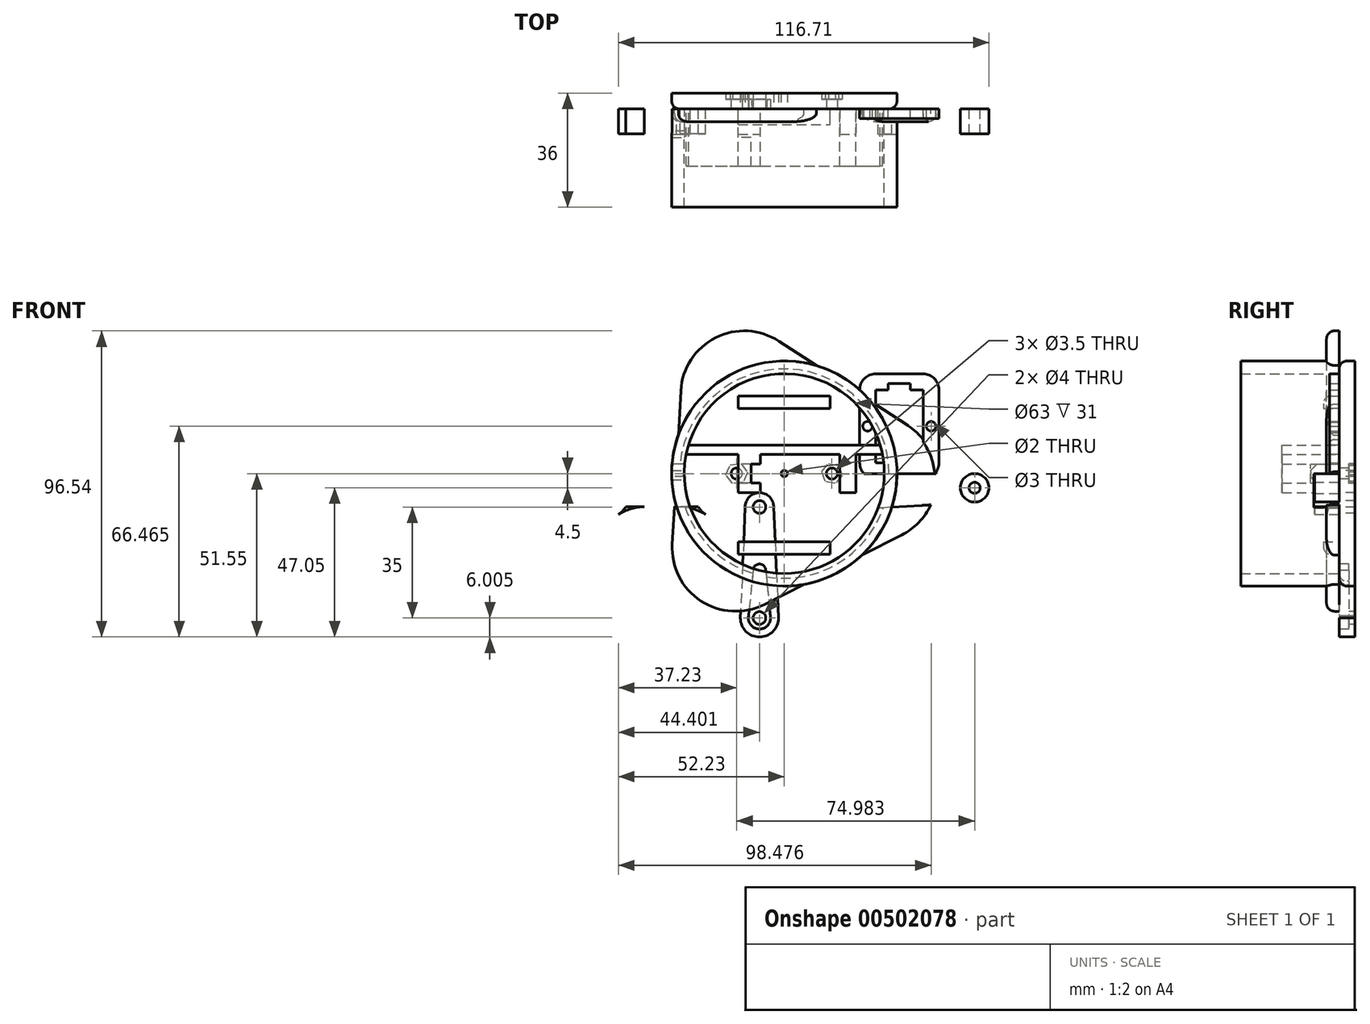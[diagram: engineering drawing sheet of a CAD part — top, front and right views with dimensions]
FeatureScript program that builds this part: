
annotation { "Feature Type Name" : "Feature", "Feature Type Description" : "" }
export const myFeature = defineFeature(function(context is Context, id is Id, definition is map)
    precondition{}
    {
        {
            var Q0;
            Q0=qCreatedBy(makeId("Front.planeOp"),FACE);
            var sketch = newSketch(context, id + "F0", { "sketchPlane" : qUnion([Q0])});
            skCircle(sketch, "E0", {"center": v(0, 0) * mm, "radius": 35.5 * mm});
            skLineSegment(sketch, "E1.bottom", {"start": v(-14.5, 24.48) * mm, "end": v(14.5, 24.48) * mm});
            skLineSegment(sketch, "E1.top", {"start": v(-14.5, 20.48) * mm, "end": v(14.5, 20.48) * mm});
            skLineSegment(sketch, "E1.left", {"start": v(-14.5, 24.48) * mm, "end": v(-14.5, 20.48) * mm});
            skLineSegment(sketch, "E1.right", {"start": v(14.5, 24.48) * mm, "end": v(14.5, 20.48) * mm});
            skLineSegment(sketch, "E2.bottom", {"start": v(-14.5, -21.52) * mm, "end": v(14.5, -21.52) * mm});
            skLineSegment(sketch, "E2.top", {"start": v(-14.5, -25.52) * mm, "end": v(14.5, -25.52) * mm});
            skLineSegment(sketch, "E2.left", {"start": v(-14.5, -21.52) * mm, "end": v(-14.5, -25.52) * mm});
            skLineSegment(sketch, "E2.right", {"start": v(14.5, -21.52) * mm, "end": v(14.5, -25.52) * mm});
            skCircle(sketch, "E3", {"center": v(0, 0) * mm, "radius": 1 * mm});
            skCircle(sketch, "E4", {"center": v(15, 0) * mm, "radius": 1.75 * mm});
            skCircle(sketch, "E5", {"center": v(-15, 0) * mm, "radius": 1.75 * mm});
            skLineSegment(sketch, "E6.0", {"start": v(17.15, 2.5) * mm, "end": v(18.24, -0.61) * mm});
            skLineSegment(sketch, "E6.1", {"start": v(18.24, -0.61) * mm, "end": v(16.09, -3.1) * mm});
            skLineSegment(sketch, "E6.2", {"start": v(16.09, -3.1) * mm, "end": v(12.85, -2.5) * mm});
            skLineSegment(sketch, "E6.3", {"start": v(12.85, -2.5) * mm, "end": v(11.76, 0.61) * mm});
            skLineSegment(sketch, "E6.4", {"start": v(11.76, 0.61) * mm, "end": v(13.91, 3.1) * mm});
            skLineSegment(sketch, "E6.5", {"start": v(13.91, 3.1) * mm, "end": v(17.15, 2.5) * mm});
            skPoint(sketch, "E6.0.midPoint", {"position": v(17.7, 0.94) * mm});
            skLineSegment(sketch, "E7.0", {"start": v(-13.66, 3.16) * mm, "end": v(-11.6, 0.41) * mm});
            skLineSegment(sketch, "E7.1", {"start": v(-11.6, 0.41) * mm, "end": v(-12.94, -2.74) * mm});
            skLineSegment(sketch, "E7.2", {"start": v(-12.94, -2.74) * mm, "end": v(-16.34, -3.16) * mm});
            skLineSegment(sketch, "E7.3", {"start": v(-16.34, -3.16) * mm, "end": v(-18.4, -0.41) * mm});
            skLineSegment(sketch, "E7.4", {"start": v(-18.4, -0.41) * mm, "end": v(-17.06, 2.74) * mm});
            skLineSegment(sketch, "E7.5", {"start": v(-17.06, 2.74) * mm, "end": v(-13.66, 3.16) * mm});
            skPoint(sketch, "E7.0.midPoint", {"position": v(-12.63, 1.78) * mm});
            skSolve(sketch);
        }
        {
            var Q0;
            Q0=makeQuery(id+"F0.imprint","IMPRINT",FACE,{"disambiguationData":[TD([[makeQuery(id+"F0.imprint","IMPRINT",EDGE,{"derivedFrom":sQuery(id+"F0.wireOp",EDGE,"E0")}),1.0]])]});
            var Q1;
            Q1=makeQuery(id+"F0.imprint","IMPRINT",FACE,{"disambiguationData":[TD([[makeQuery(id+"F0.imprint","IMPRINT",EDGE,{"derivedFrom":sQuery(id+"F0.wireOp",EDGE,"E1.bottom")}),-1.0]])]});
            var Q2;
            Q2=makeQuery(id+"F0.imprint","IMPRINT",FACE,{"disambiguationData":[TD([[makeQuery(id+"F0.imprint","IMPRINT",EDGE,{"derivedFrom":sQuery(id+"F0.wireOp",EDGE,"E2.bottom")}),-1.0]])]});
            extrude(context, id + "F1", {"entities" : qUnion([Q0, Q1, Q2]), "depth" : -5 * mm});
        }
        {
            var Q0;
            Q0=makeQuery(id+"F0.imprint","IMPRINT",FACE,{"disambiguationData":[TD([[makeQuery(id+"F0.imprint","IMPRINT",EDGE,{"derivedFrom":sQuery(id+"F0.wireOp",EDGE,"E1.bottom")}),-1.0]])]});
            var Q1;
            Q1=makeQuery(id+"F0.imprint","IMPRINT",FACE,{"disambiguationData":[TD([[makeQuery(id+"F0.imprint","IMPRINT",EDGE,{"derivedFrom":sQuery(id+"F0.wireOp",EDGE,"E2.bottom")}),-1.0]])]});
            extrude(context, id + "F2", {"entities" : qUnion([Q0, Q1]), "operationType" : NewBodyOperationType.ADD, "depth" : 5 * mm});
        }
        {
            var Q0;
            Q0=makeQuery(id+"F0.imprint","IMPRINT",FACE,{"disambiguationData":[TD([[makeQuery(id+"F0.imprint","IMPRINT",EDGE,{"derivedFrom":sQuery(id+"F0.wireOp",EDGE,"E4")}),-1.0]])]});
            var Q1;
            Q1=makeQuery(id+"F0.imprint","IMPRINT",FACE,{"disambiguationData":[TD([[makeQuery(id+"F0.imprint","IMPRINT",EDGE,{"derivedFrom":sQuery(id+"F0.wireOp",EDGE,"E5")}),-1.0]])]});
            extrude(context, id + "F3", {"entities" : qUnion([Q0, Q1]), "operationType" : NewBodyOperationType.ADD, "depth" : -3 * mm});
        }
        {
            var Q0;
            Q0=qCreatedBy(makeId("Front.planeOp"),FACE);
            var sketch = newSketch(context, id + "F4", { "sketchPlane" : qUnion([Q0])});
            skLineSegment(sketch, "E8.bottom", {"start": v(28.75, 31.42) * mm, "end": v(43.75, 31.42) * mm});
            skLineSegment(sketch, "E8.top", {"start": v(28.75, -1.58) * mm, "end": v(43.75, -1.58) * mm});
            skLineSegment(sketch, "E8.left", {"start": v(23.75, 26.42) * mm, "end": v(23.75, 3.42) * mm});
            skLineSegment(sketch, "E8.right", {"start": v(48.75, 26.42) * mm, "end": v(48.75, 3.42) * mm});
            skPoint(sketch, "E9.visualSharp", {"position": v(48.75, 31.42) * mm});
            skArc(sketch, "E9.filletArc", {"start": v(48.75, 26.42) * mm, "mid": v(47.28, 29.95) * mm, "end": v(43.75, 31.42) * mm});
            skPoint(sketch, "E10.visualSharp", {"position": v(23.75, 31.42) * mm});
            skArc(sketch, "E10.filletArc", {"start": v(28.75, 31.42) * mm, "mid": v(25.21, 29.95) * mm, "end": v(23.75, 26.42) * mm});
            skPoint(sketch, "E11.visualSharp", {"position": v(48.75, -1.58) * mm});
            skArc(sketch, "E11.filletArc", {"start": v(43.75, -1.58) * mm, "mid": v(47.28, -0.12) * mm, "end": v(48.75, 3.42) * mm});
            skPoint(sketch, "E12.visualSharp", {"position": v(23.75, -1.58) * mm});
            skArc(sketch, "E12.filletArc", {"start": v(23.75, 3.42) * mm, "mid": v(25.21, -0.12) * mm, "end": v(28.75, -1.58) * mm});
            skLineSegment(sketch, "E13", {"start": v(28.75, 26.42) * mm, "end": v(28.75, 3.42) * mm});
            skLineSegment(sketch, "E14", {"start": v(43.75, 3.42) * mm, "end": v(43.75, 26.42) * mm});
            skLineSegment(sketch, "E15", {"start": v(39.75, 26.42) * mm, "end": v(43.75, 26.42) * mm});
            skLineSegment(sketch, "E16", {"start": v(28.75, 26.42) * mm, "end": v(32.75, 26.42) * mm});
            skLineSegment(sketch, "E17", {"start": v(32.75, 26.42) * mm, "end": v(32.75, 28.42) * mm});
            skLineSegment(sketch, "E18", {"start": v(32.75, 28.42) * mm, "end": v(39.75, 28.42) * mm});
            skLineSegment(sketch, "E19", {"start": v(39.75, 28.42) * mm, "end": v(39.75, 26.42) * mm});
            skCircle(sketch, "E20", {"center": v(26.25, 14.92) * mm, "radius": 1.5 * mm});
            skPoint(sketch, "E20.centerSnap0", {"position": v(23.75, 14.92) * mm});
            skPoint(sketch, "E21.centerSnap0", {"position": v(48.75, 14.92) * mm});
            skLineSegment(sketch, "E22", {"start": v(28.75, 3.42) * mm, "end": v(43.75, 3.42) * mm});
            skCircle(sketch, "E23", {"center": v(46.25, 14.92) * mm, "radius": 1.5 * mm});
            skSolve(sketch);
        }
        {
            var Q0;
            Q0=makeQuery(id+"F4.imprint","IMPRINT",FACE,{"disambiguationData":[TD([[makeQuery(id+"F4.imprint","IMPRINT",EDGE,{"derivedFrom":sQuery(id+"F4.wireOp",EDGE,"E8.bottom")}),-1.0]])]});
            extrude(context, id + "F5", {"entities" : qUnion([Q0]), "depth" : 3 * mm});
        }
        {
            var Q0;
            Q0=qCreatedBy(makeId("Front.planeOp"),FACE);
            var sketch = newSketch(context, id + "F6", { "sketchPlane" : qUnion([Q0])});
            skCircle(sketch, "E24", {"center": v(-7.83, -45.55) * mm, "radius": 6 * mm});
            skCircle(sketch, "E25", {"center": v(-7.83, -10.55) * mm, "radius": 4.5 * mm});
            skLineSegment(sketch, "E26", {"start": v(-3.33, -10.55) * mm, "end": v(-1.83, -45.55) * mm});
            skLineSegment(sketch, "E27", {"start": v(-12.33, -10.55) * mm, "end": v(-13.83, -45.55) * mm});
            skCircle(sketch, "E28", {"center": v(-7.83, -10.55) * mm, "radius": 2 * mm});
            skCircle(sketch, "E29", {"center": v(-7.83, -45.55) * mm, "radius": 2 * mm});
            skCircle(sketch, "E30", {"center": v(-7.83, -45.55) * mm, "radius": 3.5 * mm});
            skCircle(sketch, "E31", {"center": v(-7.83, -30.55) * mm, "radius": 2 * mm});
            skLineSegment(sketch, "E32", {"start": v(-5.83, -30.55) * mm, "end": v(-4.31, -45.55) * mm});
            skLineSegment(sketch, "E33", {"start": v(-9.83, -30.55) * mm, "end": v(-11.33, -45.55) * mm});
            skCircle(sketch, "E34", {"center": v(-7.83, -30.55) * mm, "radius": 3.5 * mm});
            skLineSegment(sketch, "E35", {"start": v(-5.27, -14.25) * mm, "end": v(-4.63, -29.25) * mm});
            skLineSegment(sketch, "E36", {"start": v(-10.39, -14.25) * mm, "end": v(-11.03, -29.25) * mm});
            skSolve(sketch);
        }
        {
            var Q0;
            Q0=makeQuery(id+"F2.opExtrude","CAP_EDGE",EDGE,{"disambiguationData":[OSD([sQuery(id+"F0.wireOp",EDGE,"E2.top")])],"isStart":false});
            var Q1;
            Q1=makeQuery(id+"F2.opExtrude","CAP_EDGE",EDGE,{"disambiguationData":[OSD([sQuery(id+"F0.wireOp",EDGE,"E2.top")])],"isStart":true});
            fillet(context, id + "F7", {"entities" : qUnion([Q0, Q1]), "radius" : 2.5 * mm, "tangentPropagation" : true, "allowEdgeOverflow" : false});
        }
        {
            var Q0;
            Q0=makeQuery(id+"F2.opExtrude","CAP_EDGE",EDGE,{"disambiguationData":[OSD([sQuery(id+"F0.wireOp",EDGE,"E1.bottom")])],"isStart":false});
            var Q1;
            Q1=makeQuery(id+"F2.opExtrude","CAP_EDGE",EDGE,{"disambiguationData":[OSD([sQuery(id+"F0.wireOp",EDGE,"E1.bottom")])],"isStart":true});
            fillet(context, id + "F8", {"entities" : qUnion([Q0, Q1]), "radius" : 2.5 * mm, "tangentPropagation" : true, "allowEdgeOverflow" : false});
        }
        {
            var Q0;
            Q0=makeQuery(id+"F1.opExtrude","CAP_EDGE",EDGE,{"disambiguationData":[OSD([sQuery(id+"F0.wireOp",EDGE,"E0")])],"isStart":true});
            fillet(context, id + "F9", {"entities" : qUnion([Q0]), "radius" : 2.5 * mm, "tangentPropagation" : true, "allowEdgeOverflow" : false});
        }
        {
            var Q0;
            Q0=qCreatedBy(makeId("Front.planeOp"),FACE);
            var sketch = newSketch(context, id + "F10", { "sketchPlane" : qUnion([Q0])});
            skCircle(sketch, "E37", {"center": v(0, 0) * mm, "radius": 31.5 * mm});
            skCircle(sketch, "E38", {"center": v(0, 0) * mm, "radius": 35.5 * mm});
            skLineSegment(sketch, "E39", {"start": v(30.19, -9) * mm, "end": v(-30.19, -9) * mm});
            skLineSegment(sketch, "E40.bottom", {"start": v(-30.19, 9) * mm, "end": v(30.19, 9) * mm});
            skLineSegment(sketch, "E40.top", {"start": v(-30.92, 6) * mm, "end": v(30.92, 6) * mm});
            skLineSegment(sketch, "E41.bottom", {"start": v(-30.19, -9) * mm, "end": v(30.19, -9) * mm});
            skLineSegment(sketch, "E41.top", {"start": v(-30.92, -6) * mm, "end": v(30.92, -6) * mm});
            skLineSegment(sketch, "E42", {"start": v(31.5, 0) * mm, "end": v(22.5, 0) * mm});
            skLineSegment(sketch, "E43", {"start": v(22.5, 0) * mm, "end": v(22.5, 6) * mm});
            skLineSegment(sketch, "E44", {"start": v(22.5, 0) * mm, "end": v(22.5, -6) * mm});
            skLineSegment(sketch, "E45", {"start": v(17.5, 6) * mm, "end": v(17.5, -6) * mm});
            skLineSegment(sketch, "E46", {"start": v(-31.5, 0) * mm, "end": v(-14.5, 0) * mm});
            skLineSegment(sketch, "E47", {"start": v(-14.5, 0) * mm, "end": v(-14.5, 6) * mm});
            skLineSegment(sketch, "E48", {"start": v(-14.5, 0) * mm, "end": v(-14.5, -6) * mm});
            skLineSegment(sketch, "E49", {"start": v(-10.5, 6) * mm, "end": v(-10.5, -6) * mm});
            skLineSegment(sketch, "E50", {"start": v(-7.5, 6) * mm, "end": v(-7.5, 3) * mm});
            skLineSegment(sketch, "E51", {"start": v(-7.5, 3) * mm, "end": v(-10.5, 3) * mm});
            skLineSegment(sketch, "E52", {"start": v(-10.5, -3) * mm, "end": v(-7.5, -3) * mm});
            skLineSegment(sketch, "E53", {"start": v(-7.5, -3) * mm, "end": v(-7.5, -6) * mm});
            skLineSegment(sketch, "E54", {"start": v(-10.5, 3) * mm, "end": v(-14.5, 3) * mm});
            skLineSegment(sketch, "E55", {"start": v(-10.5, -3) * mm, "end": v(-14.5, -3) * mm});
            skLineSegment(sketch, "E56", {"start": v(-31.36, 3) * mm, "end": v(-35.37, 3) * mm});
            skLineSegment(sketch, "E57", {"start": v(-31.36, -3) * mm, "end": v(-35.37, -3) * mm});
            skSolve(sketch);
        }
        {
            var Q0;
            Q0=makeQuery(id+"F10.imprint","IMPRINT",FACE,{"disambiguationData":[TD([[makeQuery(id+"F10.imprint","IMPRINT",EDGE,{"derivedFrom":sQuery(id+"F10.wireOp",EDGE,"E38")}),1.0]])]});
            var Q1;
            {var subQ10=sQuery(id+"F10.wireOp",EDGE,"E56");Q1=makeQuery(id+"F10.imprint","IMPRINT",FACE,{"disambiguationData":[TD([[makeQuery(id+"F10.imprint","IMPRINT",EDGE,{"derivedFrom":subQ10}),-1.0]])]});}
            extrude(context, id + "F11", {"entities" : qUnion([Q0, Q1]), "depth" : 31 * mm, "offsetDistance" : 25 * mm});
        }
        {
            var Q0;
            {var subQ4=sQuery(id+"F10.wireOp",EDGE,"E40.bottom");Q0=makeQuery(id+"F10.imprint","IMPRINT",FACE,{"disambiguationData":[TD([[makeQuery(id+"F10.imprint","IMPRINT",EDGE,{"derivedFrom":subQ4}),-1.0]])]});}
            var Q1;
            {var subQ4=sQuery(id+"F10.wireOp",EDGE,"E41.bottom");Q1=makeQuery(id+"F10.imprint","IMPRINT",FACE,{"disambiguationData":[TD([[makeQuery(id+"F10.imprint","IMPRINT",EDGE,{"derivedFrom":subQ4}),1.0]])]});}
            var Q2;
            {var subQ1=sQuery(id+"F10.wireOp",EDGE,"E43");Q2=makeQuery(id+"F10.imprint","IMPRINT",FACE,{"disambiguationData":[TD([[makeQuery(id+"F10.imprint","IMPRINT",EDGE,{"derivedFrom":subQ1}),1.0]])]});}
            var Q3;
            {var subQ4=sQuery(id+"F10.wireOp",EDGE,"E47");Q3=makeQuery(id+"F10.imprint","IMPRINT",FACE,{"disambiguationData":[TD([[makeQuery(id+"F10.imprint","IMPRINT",EDGE,{"derivedFrom":subQ4}),-1.0]])]});}
            var Q4;
            {var subQ3=sQuery(id+"F10.wireOp",EDGE,"E50");Q4=makeQuery(id+"F10.imprint","IMPRINT",FACE,{"disambiguationData":[TD([[makeQuery(id+"F10.imprint","IMPRINT",EDGE,{"derivedFrom":subQ3}),-1.0]])]});}
            var Q5;
            {var subQ4=sQuery(id+"F10.wireOp",EDGE,"E52");Q5=makeQuery(id+"F10.imprint","IMPRINT",FACE,{"disambiguationData":[TD([[makeQuery(id+"F10.imprint","IMPRINT",EDGE,{"derivedFrom":subQ4}),-1.0]])]});}
            var Q6;
            {var subQ5=sQuery(id+"F10.wireOp",EDGE,"E55");Q6=makeQuery(id+"F10.imprint","IMPRINT",FACE,{"disambiguationData":[TD([[makeQuery(id+"F10.imprint","IMPRINT",EDGE,{"derivedFrom":subQ5}),1.0]])]});}
            var Q7;
            {var subQ0=sQuery(id+"F10.wireOp",EDGE,"E54");Q7=makeQuery(id+"F10.imprint","IMPRINT",FACE,{"disambiguationData":[TD([[makeQuery(id+"F10.imprint","IMPRINT",EDGE,{"derivedFrom":subQ0}),1.0]])]});}
            extrude(context, id + "F12", {"entities" : qUnion([Q0, Q1, Q2, Q3, Q4, Q5, Q6, Q7]), "operationType" : NewBodyOperationType.ADD, "depth" : 18 * mm, "offsetDistance" : 25 * mm});
        }
        {
            var Q0;
            {var subQ0=sQuery(id+"F10.wireOp",EDGE,"E54");Q0=makeQuery(id+"F10.imprint","IMPRINT",FACE,{"disambiguationData":[TD([[makeQuery(id+"F10.imprint","IMPRINT",EDGE,{"derivedFrom":subQ0}),1.0]])]});}
            extrude(context, id + "F13", {"entities" : qUnion([Q0]), "operationType" : NewBodyOperationType.REMOVE, "oppositeDirection" : true, "depth" : -9 * mm, "offsetDistance" : 25 * mm});
        }
        {
            var Q0;
            {var subQ0=sQuery(id+"F10.wireOp",EDGE,"E56");Q0=makeQuery(id+"F10.imprint","IMPRINT",FACE,{"disambiguationData":[TD([[makeQuery(id+"F10.imprint","IMPRINT",EDGE,{"derivedFrom":subQ0}),1.0]])]});}
            extrude(context, id + "F14", {"entities" : qUnion([Q0]), "operationType" : NewBodyOperationType.REMOVE, "oppositeDirection" : true, "depth" : -9 * mm, "offsetDistance" : 25 * mm});
        }
        {
            var Q0;
            Q0=makeQuery(id+"F14.boolean.opBoolean","COPY",EDGE,{"derivedFrom":makeQuery(id+"F14.opExtrude","CAP_EDGE",EDGE,{"disambiguationData":[OSD([sQuery(id+"F10.wireOp",EDGE,"E56")])],"isStart":false})});
            var Q1;
            Q1=makeQuery(id+"F14.boolean.opBoolean","COPY",EDGE,{"derivedFrom":makeQuery(id+"F14.opExtrude","CAP_EDGE",EDGE,{"disambiguationData":[OSD([sQuery(id+"F10.wireOp",EDGE,"E57")])],"isStart":false})});
            chamfer(context, id + "F15", {"entities" : qUnion([Q0, Q1]), "width" : 2 * mm, "tangentPropagation" : true});
        }
        {
            var Q0;
            {var subQ10=sQuery(id+"F10.wireOp",EDGE,"E56");Q0=makeQuery(id+"F10.imprint","IMPRINT",FACE,{"disambiguationData":[TD([[makeQuery(id+"F10.imprint","IMPRINT",EDGE,{"derivedFrom":subQ10}),-1.0]])]});}
            var sketch = newSketch(context, id + "F16", { "sketchPlane" : qUnion([Q0])});
            skCircle(sketch, "E58", {"center": v(0, 0) * mm, "radius": 34 * mm});
            skCircle(sketch, "E59.cCircle", {"center": v(0, 0) * mm, "radius": 34 * mm, "construction": true});
            skLineSegment(sketch, "E59.0", {"start": v(-35.3, -22.32) * mm, "end": v(-32.6, 26.1) * mm});
            skLineSegment(sketch, "E59.1", {"start": v(-1.68, 41.73) * mm, "end": v(38.9, 15.18) * mm});
            skLineSegment(sketch, "E59.2", {"start": v(36.98, -19.41) * mm, "end": v(-6.3, -41.28) * mm});
            skPoint(sketch, "E59.0.midPoint", {"position": v(-33.95, 1.9) * mm});
            skPoint(sketch, "E60.visualSharp", {"position": v(-30.67, 60.7) * mm});
            skArc(sketch, "E60.filletArc", {"start": v(-1.68, 41.73) * mm, "mid": v(-21.65, 42.84) * mm, "end": v(-32.6, 26.1) * mm});
            skPoint(sketch, "E61.visualSharp", {"position": v(-37.23, -56.9) * mm});
            skArc(sketch, "E61.filletArc", {"start": v(-35.3, -22.32) * mm, "mid": v(-26.28, -40.17) * mm, "end": v(-6.3, -41.28) * mm});
            skPoint(sketch, "E62.visualSharp", {"position": v(67.9, -3.79) * mm});
            skArc(sketch, "E62.filletArc", {"start": v(36.98, -19.41) * mm, "mid": v(47.93, -2.67) * mm, "end": v(38.9, 15.18) * mm});
            skSolve(sketch);
        }
        {
            var Q0;
            {var subQ0=sQuery(id+"F16.wireOp",EDGE,"E60.filletArc");Q0=makeQuery(id+"F16.imprint","IMPRINT",FACE,{"disambiguationData":[TD([[makeQuery(id+"F16.imprint","IMPRINT",EDGE,{"derivedFrom":subQ0}),1.0]])]});}
            var Q1;
            {var subQ0=sQuery(id+"F16.wireOp",EDGE,"E62.filletArc");Q1=makeQuery(id+"F16.imprint","IMPRINT",FACE,{"disambiguationData":[TD([[makeQuery(id+"F16.imprint","IMPRINT",EDGE,{"derivedFrom":subQ0}),1.0]])]});}
            var Q2;
            {var subQ0=sQuery(id+"F16.wireOp",EDGE,"E61.filletArc");Q2=makeQuery(id+"F16.imprint","IMPRINT",FACE,{"disambiguationData":[TD([[makeQuery(id+"F16.imprint","IMPRINT",EDGE,{"derivedFrom":subQ0}),1.0]])]});}
            extrude(context, id + "F17", {"entities" : qUnion([Q0, Q1, Q2]), "operationType" : NewBodyOperationType.ADD, "depth" : 4 * mm, "offsetDistance" : 25 * mm});
        }
        {
            var Q0;
            Q0=makeQuery(id+"F17.opExtrude","CAP_EDGE",EDGE,{"disambiguationData":[OSD([sQuery(id+"F16.wireOp",EDGE,"E62.filletArc")])],"isStart":false});
            var Q1;
            Q1=makeQuery(id+"F17.opExtrude","CAP_EDGE",EDGE,{"disambiguationData":[OSD([sQuery(id+"F16.wireOp",EDGE,"E61.filletArc")])],"isStart":false});
            var Q2;
            Q2=makeQuery(id+"F17.opExtrude","CAP_EDGE",EDGE,{"disambiguationData":[OSD([sQuery(id+"F16.wireOp",EDGE,"E60.filletArc")])],"isStart":false});
            fillet(context, id + "F18", {"entities" : qUnion([Q0, Q1, Q2]), "radius" : 2.5 * mm, "tangentPropagation" : true, "allowEdgeOverflow" : false});
        }
        {
            var Q0;
            {var subQ1=sQuery(id+"F6.wireOp",EDGE,"E24");var subQ5=sQuery(id+"F6.wireOp",EDGE,"E27");var subQ6=makeQuery(id+"F6.imprint","INTERSECT",VERTEX,{"disambiguationData":[OD(1.0)],"derivedFrom":[subQ1,subQ5]});Q0=makeQuery(id+"F6.imprint","IMPRINT",FACE,{"disambiguationData":[TD([[makeQuery(id+"F6.imprint","IMPRINT",EDGE,{"disambiguationData":[TD([[subQ6,1.0]])],"derivedFrom":subQ1}),-1.0]])]});}
            var Q1;
            {var subQ0=sQuery(id+"F6.wireOp",EDGE,"E26");var subQ1=sQuery(id+"F6.wireOp",EDGE,"E24");var subQ8=makeQuery(id+"F6.imprint","INTERSECT",VERTEX,{"disambiguationData":[OD(1.0)],"derivedFrom":[subQ1,subQ0]});Q1=makeQuery(id+"F6.imprint","IMPRINT",FACE,{"disambiguationData":[TD([[makeQuery(id+"F6.imprint","IMPRINT",EDGE,{"disambiguationData":[TD([[subQ8,-1.0]])],"derivedFrom":subQ1}),1.0]])]});}
            var Q2;
            {var subQ1=sQuery(id+"F6.wireOp",EDGE,"E24");var subQ5=sQuery(id+"F6.wireOp",EDGE,"E26");var subQ8=makeQuery(id+"F6.imprint","INTERSECT",VERTEX,{"disambiguationData":[OD(1.0)],"derivedFrom":[subQ1,subQ5]});Q2=makeQuery(id+"F6.imprint","IMPRINT",FACE,{"disambiguationData":[TD([[makeQuery(id+"F6.imprint","IMPRINT",EDGE,{"disambiguationData":[TD([[subQ8,-1.0]])],"derivedFrom":subQ1}),-1.0]])]});}
            var Q3;
            Q3=makeQuery(id+"F6.imprint","IMPRINT",FACE,{"disambiguationData":[TD([[makeQuery(id+"F6.imprint","IMPRINT",EDGE,{"derivedFrom":sQuery(id+"F6.wireOp",EDGE,"E28")}),-1.0]])]});
            var Q4;
            {var subQ3=sQuery(id+"F6.wireOp",EDGE,"E32");var subQ4=sQuery(id+"F6.wireOp",EDGE,"E31");var subQ5=makeQuery(id+"F6.imprint","INTERSECT",VERTEX,{"derivedFrom":[subQ4,subQ3]});Q4=makeQuery(id+"F6.imprint","IMPRINT",FACE,{"disambiguationData":[TD([[makeQuery(id+"F6.imprint","IMPRINT",EDGE,{"disambiguationData":[TD([[subQ5,-1.0]])],"derivedFrom":subQ4}),-1.0]])]});}
            var Q5;
            {var subQ0=sQuery(id+"F6.wireOp",EDGE,"E32");var subQ1=sQuery(id+"F6.wireOp",EDGE,"E24");var subQ2=makeQuery(id+"F6.imprint","INTERSECT",VERTEX,{"derivedFrom":[subQ1,subQ0]});Q5=makeQuery(id+"F6.imprint","IMPRINT",FACE,{"disambiguationData":[TD([[makeQuery(id+"F6.imprint","IMPRINT",EDGE,{"disambiguationData":[TD([[subQ2,-1.0]])],"derivedFrom":subQ1}),1.0]])]});}
            var Q6;
            {var subQ0=sQuery(id+"F6.wireOp",EDGE,"E32");var subQ1=sQuery(id+"F6.wireOp",EDGE,"E24");var subQ2=makeQuery(id+"F6.imprint","INTERSECT",VERTEX,{"derivedFrom":[subQ1,subQ0]});Q6=makeQuery(id+"F6.imprint","IMPRINT",FACE,{"disambiguationData":[TD([[makeQuery(id+"F6.imprint","IMPRINT",EDGE,{"disambiguationData":[TD([[subQ2,-1.0]])],"derivedFrom":subQ1}),-1.0]])]});}
            var Q7;
            {var subQ0=sQuery(id+"F6.wireOp",EDGE,"E31");var subQ1=makeQuery(id+"F6.imprint","INTERSECT",VERTEX,{"derivedFrom":[subQ0,sQuery(id+"F6.wireOp",EDGE,"E32")]});Q7=makeQuery(id+"F6.imprint","IMPRINT",FACE,{"disambiguationData":[TD([[makeQuery(id+"F6.imprint","IMPRINT",EDGE,{"disambiguationData":[TD([[subQ1,-1.0]])],"derivedFrom":subQ0}),1.0]])]});}
            var Q8;
            {var subQ0=sQuery(id+"F6.wireOp",EDGE,"E32");var subQ1=sQuery(id+"F6.wireOp",EDGE,"E31");var subQ2=makeQuery(id+"F6.imprint","INTERSECT",VERTEX,{"derivedFrom":[subQ1,subQ0]});Q8=makeQuery(id+"F6.imprint","IMPRINT",FACE,{"disambiguationData":[TD([[makeQuery(id+"F6.imprint","IMPRINT",EDGE,{"disambiguationData":[TD([[subQ2,1.0]])],"derivedFrom":subQ1}),-1.0]])]});}
            var Q9;
            {var subQ0=sQuery(id+"F6.wireOp",EDGE,"E35");var subQ1=sQuery(id+"F6.wireOp",EDGE,"E25");var subQ2=makeQuery(id+"F6.imprint","INTERSECT",VERTEX,{"derivedFrom":[subQ1,subQ0]});Q9=makeQuery(id+"F6.imprint","IMPRINT",FACE,{"disambiguationData":[TD([[makeQuery(id+"F6.imprint","IMPRINT",EDGE,{"disambiguationData":[TD([[subQ2,1.0]])],"derivedFrom":subQ1}),-1.0]])]});}
            var Q10;
            Q10=makeQuery(id+"F6.imprint","IMPRINT",FACE,{"disambiguationData":[TD([[makeQuery(id+"F6.imprint","IMPRINT",EDGE,{"derivedFrom":sQuery(id+"F6.wireOp",EDGE,"E29")}),-1.0]])]});
            extrude(context, id + "F19", {"entities" : qUnion([Q0, Q1, Q2, Q3, Q4, Q5, Q6, Q7, Q8, Q9, Q10]), "depth" : -5 * mm, "offsetDistance" : 25 * mm});
        }
        {
            var Q0;
            {var subQ0=sQuery(id+"F6.wireOp",EDGE,"E32");var subQ1=sQuery(id+"F6.wireOp",EDGE,"E24");var subQ2=makeQuery(id+"F6.imprint","INTERSECT",VERTEX,{"derivedFrom":[subQ1,subQ0]});Q0=makeQuery(id+"F6.imprint","IMPRINT",FACE,{"disambiguationData":[TD([[makeQuery(id+"F6.imprint","IMPRINT",EDGE,{"disambiguationData":[TD([[subQ2,-1.0]])],"derivedFrom":subQ1}),-1.0]])]});}
            var Q1;
            {var subQ0=sQuery(id+"F6.wireOp",EDGE,"E32");var subQ1=sQuery(id+"F6.wireOp",EDGE,"E24");var subQ2=makeQuery(id+"F6.imprint","INTERSECT",VERTEX,{"derivedFrom":[subQ1,subQ0]});Q1=makeQuery(id+"F6.imprint","IMPRINT",FACE,{"disambiguationData":[TD([[makeQuery(id+"F6.imprint","IMPRINT",EDGE,{"disambiguationData":[TD([[subQ2,-1.0]])],"derivedFrom":subQ1}),1.0]])]});}
            var Q2;
            Q2=makeQuery(id+"F6.imprint","IMPRINT",FACE,{"disambiguationData":[TD([[makeQuery(id+"F6.imprint","IMPRINT",EDGE,{"derivedFrom":sQuery(id+"F6.wireOp",EDGE,"E29")}),-1.0]])]});
            var Q3;
            {var subQ0=sQuery(id+"F6.wireOp",EDGE,"E32");var subQ1=sQuery(id+"F6.wireOp",EDGE,"E31");var subQ2=makeQuery(id+"F6.imprint","INTERSECT",VERTEX,{"derivedFrom":[subQ1,subQ0]});Q3=makeQuery(id+"F6.imprint","IMPRINT",FACE,{"disambiguationData":[TD([[makeQuery(id+"F6.imprint","IMPRINT",EDGE,{"disambiguationData":[TD([[subQ2,1.0]])],"derivedFrom":subQ1}),-1.0]])]});}
            var Q4;
            {var subQ0=sQuery(id+"F6.wireOp",EDGE,"E31");var subQ1=makeQuery(id+"F6.imprint","INTERSECT",VERTEX,{"derivedFrom":[subQ0,sQuery(id+"F6.wireOp",EDGE,"E32")]});Q4=makeQuery(id+"F6.imprint","IMPRINT",FACE,{"disambiguationData":[TD([[makeQuery(id+"F6.imprint","IMPRINT",EDGE,{"disambiguationData":[TD([[subQ1,-1.0]])],"derivedFrom":subQ0}),1.0]])]});}
            extrude(context, id + "F20", {"entities" : qUnion([Q0, Q1, Q2, Q3, Q4]), "operationType" : NewBodyOperationType.REMOVE, "oppositeDirection" : true, "depth" : 3 * mm, "offsetDistance" : 25 * mm});
        }
        {
            var Q0;
            Q0=qCreatedBy(makeId("Front.planeOp"),FACE);
            var sketch = newSketch(context, id + "F21", { "sketchPlane" : qUnion([Q0])});
            skLineSegment(sketch, "E63", {"start": v(-56.02, 0) * mm, "end": v(59.98, 0) * mm});
            skCircle(sketch, "E64", {"center": v(-56.02, -7) * mm, "radius": 7 * mm});
            skCircle(sketch, "E65", {"center": v(-56.02, -7) * mm, "radius": 1.75 * mm});
            skCircle(sketch, "E66", {"center": v(-21.02, -7.04) * mm, "radius": 7 * mm});
            skCircle(sketch, "E67", {"center": v(-21.02, -7.04) * mm, "radius": 1.75 * mm});
            skCircle(sketch, "E68", {"center": v(59.98, -4.5) * mm, "radius": 4.5 * mm});
            skLineSegment(sketch, "E69", {"start": v(59.98, -9) * mm, "end": v(-21.02, -14.04) * mm});
            skCircle(sketch, "E70", {"center": v(59.98, -4.5) * mm, "radius": 1.75 * mm});
            skLineSegment(sketch, "E71", {"start": v(-48.02, -7) * mm, "end": v(-29.02, -7) * mm});
            skLineSegment(sketch, "E72", {"start": v(-48.02, -3) * mm, "end": v(-29.02, -3) * mm});
            skCircle(sketch, "E73", {"center": v(-48.02, -5) * mm, "radius": 2 * mm});
            skCircle(sketch, "E74", {"center": v(-29.02, -5) * mm, "radius": 2 * mm});
            skLineSegment(sketch, "E75", {"start": v(-49.95, -10.5) * mm, "end": v(-27.1, -10.5) * mm});
            skSolve(sketch);
        }
        {
            var Q0;
            {var subQ1=sQuery(id+"F21.wireOp",EDGE,"E63");Q0=makeQuery(id+"F21.imprint","IMPRINT",FACE,{"disambiguationData":[TD([[makeQuery(id+"F21.imprint","IMPRINT",EDGE,{"derivedFrom":subQ1}),-1.0]])]});}
            var Q1;
            {var subQ1=sQuery(id+"F21.wireOp",EDGE,"E71");Q1=makeQuery(id+"F21.imprint","IMPRINT",FACE,{"disambiguationData":[TD([[makeQuery(id+"F21.imprint","IMPRINT",EDGE,{"derivedFrom":subQ1}),-1.0]])]});}
            var Q2;
            Q2=makeQuery(id+"F21.imprint","IMPRINT",FACE,{"disambiguationData":[TD([[makeQuery(id+"F21.imprint","IMPRINT",EDGE,{"derivedFrom":sQuery(id+"F21.wireOp",EDGE,"E65")}),-1.0]])]});
            var Q3;
            {var subQ0=sQuery(id+"F21.wireOp",EDGE,"E71");Q3=makeQuery(id+"F21.imprint","IMPRINT",FACE,{"disambiguationData":[TD([[makeQuery(id+"F21.imprint","IMPRINT",EDGE,{"derivedFrom":subQ0}),1.0]])]});}
            var Q4;
            {var subQ0=sQuery(id+"F21.wireOp",EDGE,"E74");var subQ1=sQuery(id+"F21.wireOp",EDGE,"E66");var subQ2=makeQuery(id+"F21.imprint","INTERSECT",VERTEX,{"disambiguationData":[OD(0.0)],"derivedFrom":[subQ1,subQ0]});Q4=makeQuery(id+"F21.imprint","IMPRINT",FACE,{"disambiguationData":[TD([[makeQuery(id+"F21.imprint","IMPRINT",EDGE,{"disambiguationData":[TD([[subQ2,1.0]])],"derivedFrom":subQ1}),-1.0]])]});}
            var Q5;
            {var subQ0=sQuery(id+"F21.wireOp",EDGE,"E73");var subQ1=sQuery(id+"F21.wireOp",EDGE,"E64");var subQ2=makeQuery(id+"F21.imprint","INTERSECT",VERTEX,{"disambiguationData":[OD(0.0)],"derivedFrom":[subQ1,subQ0]});Q5=makeQuery(id+"F21.imprint","IMPRINT",FACE,{"disambiguationData":[TD([[makeQuery(id+"F21.imprint","IMPRINT",EDGE,{"disambiguationData":[TD([[subQ2,1.0]])],"derivedFrom":subQ1}),-1.0]])]});}
            var Q6;
            {var subQ0=sQuery(id+"F21.wireOp",EDGE,"E73");var subQ1=sQuery(id+"F21.wireOp",EDGE,"E64");var subQ2=makeQuery(id+"F21.imprint","INTERSECT",VERTEX,{"disambiguationData":[OD(0.0)],"derivedFrom":[subQ1,subQ0]});Q6=makeQuery(id+"F21.imprint","IMPRINT",FACE,{"disambiguationData":[TD([[makeQuery(id+"F21.imprint","IMPRINT",EDGE,{"disambiguationData":[TD([[subQ2,1.0]])],"derivedFrom":subQ1}),1.0]])]});}
            var Q7;
            Q7=makeQuery(id+"F21.imprint","IMPRINT",FACE,{"disambiguationData":[TD([[makeQuery(id+"F21.imprint","IMPRINT",EDGE,{"derivedFrom":sQuery(id+"F21.wireOp",EDGE,"E67")}),-1.0]])]});
            var Q8;
            {var subQ0=sQuery(id+"F21.wireOp",EDGE,"E74");var subQ1=sQuery(id+"F21.wireOp",EDGE,"E66");var subQ2=makeQuery(id+"F21.imprint","INTERSECT",VERTEX,{"disambiguationData":[OD(0.0)],"derivedFrom":[subQ1,subQ0]});Q8=makeQuery(id+"F21.imprint","IMPRINT",FACE,{"disambiguationData":[TD([[makeQuery(id+"F21.imprint","IMPRINT",EDGE,{"disambiguationData":[TD([[subQ2,1.0]])],"derivedFrom":subQ1}),1.0]])]});}
            var Q9;
            Q9=makeQuery(id+"F21.imprint","IMPRINT",FACE,{"disambiguationData":[TD([[makeQuery(id+"F21.imprint","IMPRINT",EDGE,{"derivedFrom":sQuery(id+"F21.wireOp",EDGE,"E70")}),-1.0]])]});
            extrude(context, id + "F22", {"entities" : qUnion([Q0, Q1, Q2, Q3, Q4, Q5, Q6, Q7, Q8, Q9]), "depth" : 7.8 * mm, "offsetDistance" : 25 * mm});
        }
        {
            var Q0;
            Q0=makeQuery(id+"F22.opExtrude","SWEPT_EDGE",EDGE,{"disambiguationData":[OSD([sQuery(id+"F21.wireOp",EDGE,"E64"),sQuery(id+"F21.wireOp",EDGE,"E75")])]});
            var Q1;
            Q1=makeQuery(id+"F22.opExtrude","SWEPT_EDGE",EDGE,{"disambiguationData":[OSD([sQuery(id+"F21.wireOp",EDGE,"E66"),sQuery(id+"F21.wireOp",EDGE,"E75")])]});
            fillet(context, id + "F23", {"entities" : qUnion([Q0, Q1]), "radius" : 15 * mm, "tangentPropagation" : true, "allowEdgeOverflow" : false});
        }
        {
            var Q0;
            {var subQ0=sQuery(id+"F21.wireOp",EDGE,"E74");var subQ1=sQuery(id+"F21.wireOp",EDGE,"E66");var subQ2=makeQuery(id+"F21.imprint","INTERSECT",VERTEX,{"disambiguationData":[OD(0.0)],"derivedFrom":[subQ1,subQ0]});Q0=makeQuery(id+"F21.imprint","IMPRINT",FACE,{"disambiguationData":[TD([[makeQuery(id+"F21.imprint","IMPRINT",EDGE,{"disambiguationData":[TD([[subQ2,1.0]])],"derivedFrom":subQ1}),-1.0]])]});}
            var Q1;
            {var subQ0=sQuery(id+"F21.wireOp",EDGE,"E71");Q1=makeQuery(id+"F21.imprint","IMPRINT",FACE,{"disambiguationData":[TD([[makeQuery(id+"F21.imprint","IMPRINT",EDGE,{"derivedFrom":subQ0}),1.0]])]});}
            var Q2;
            {var subQ0=sQuery(id+"F21.wireOp",EDGE,"E73");var subQ1=sQuery(id+"F21.wireOp",EDGE,"E64");var subQ2=makeQuery(id+"F21.imprint","INTERSECT",VERTEX,{"disambiguationData":[OD(0.0)],"derivedFrom":[subQ1,subQ0]});Q2=makeQuery(id+"F21.imprint","IMPRINT",FACE,{"disambiguationData":[TD([[makeQuery(id+"F21.imprint","IMPRINT",EDGE,{"disambiguationData":[TD([[subQ2,1.0]])],"derivedFrom":subQ1}),-1.0]])]});}
            var Q3;
            {var subQ0=sQuery(id+"F21.wireOp",EDGE,"E74");var subQ1=sQuery(id+"F21.wireOp",EDGE,"E66");var subQ2=makeQuery(id+"F21.imprint","INTERSECT",VERTEX,{"disambiguationData":[OD(0.0)],"derivedFrom":[subQ1,subQ0]});Q3=makeQuery(id+"F21.imprint","IMPRINT",FACE,{"disambiguationData":[TD([[makeQuery(id+"F21.imprint","IMPRINT",EDGE,{"disambiguationData":[TD([[subQ2,1.0]])],"derivedFrom":subQ1}),1.0]])]});}
            var Q4;
            {var subQ0=sQuery(id+"F21.wireOp",EDGE,"E73");var subQ1=sQuery(id+"F21.wireOp",EDGE,"E64");var subQ2=makeQuery(id+"F21.imprint","INTERSECT",VERTEX,{"disambiguationData":[OD(0.0)],"derivedFrom":[subQ1,subQ0]});Q4=makeQuery(id+"F21.imprint","IMPRINT",FACE,{"disambiguationData":[TD([[makeQuery(id+"F21.imprint","IMPRINT",EDGE,{"disambiguationData":[TD([[subQ2,1.0]])],"derivedFrom":subQ1}),1.0]])]});}
            extrude(context, id + "F24", {"entities" : qUnion([Q0, Q1, Q2, Q3, Q4]), "operationType" : NewBodyOperationType.REMOVE, "oppositeDirection" : true, "depth" : -2 * mm, "offsetDistance" : 25 * mm});
        }
        {
            var Q0;
            {var subQ0=sQuery(id+"F21.wireOp",EDGE,"E71");Q0=makeQuery(id+"F21.imprint","IMPRINT",FACE,{"disambiguationData":[TD([[makeQuery(id+"F21.imprint","IMPRINT",EDGE,{"derivedFrom":subQ0}),1.0]])]});}
            var Q1;
            {var subQ0=sQuery(id+"F21.wireOp",EDGE,"E73");var subQ1=sQuery(id+"F21.wireOp",EDGE,"E64");var subQ2=makeQuery(id+"F21.imprint","INTERSECT",VERTEX,{"disambiguationData":[OD(0.0)],"derivedFrom":[subQ1,subQ0]});Q1=makeQuery(id+"F21.imprint","IMPRINT",FACE,{"disambiguationData":[TD([[makeQuery(id+"F21.imprint","IMPRINT",EDGE,{"disambiguationData":[TD([[subQ2,1.0]])],"derivedFrom":subQ1}),-1.0]])]});}
            var Q2;
            {var subQ0=sQuery(id+"F21.wireOp",EDGE,"E73");var subQ1=sQuery(id+"F21.wireOp",EDGE,"E64");var subQ2=makeQuery(id+"F21.imprint","INTERSECT",VERTEX,{"disambiguationData":[OD(0.0)],"derivedFrom":[subQ1,subQ0]});Q2=makeQuery(id+"F21.imprint","IMPRINT",FACE,{"disambiguationData":[TD([[makeQuery(id+"F21.imprint","IMPRINT",EDGE,{"disambiguationData":[TD([[subQ2,1.0]])],"derivedFrom":subQ1}),1.0]])]});}
            var Q3;
            {var subQ0=sQuery(id+"F21.wireOp",EDGE,"E74");var subQ1=sQuery(id+"F21.wireOp",EDGE,"E66");var subQ2=makeQuery(id+"F21.imprint","INTERSECT",VERTEX,{"disambiguationData":[OD(0.0)],"derivedFrom":[subQ1,subQ0]});Q3=makeQuery(id+"F21.imprint","IMPRINT",FACE,{"disambiguationData":[TD([[makeQuery(id+"F21.imprint","IMPRINT",EDGE,{"disambiguationData":[TD([[subQ2,1.0]])],"derivedFrom":subQ1}),-1.0]])]});}
            var Q4;
            {var subQ0=sQuery(id+"F21.wireOp",EDGE,"E74");var subQ1=sQuery(id+"F21.wireOp",EDGE,"E66");var subQ2=makeQuery(id+"F21.imprint","INTERSECT",VERTEX,{"disambiguationData":[OD(0.0)],"derivedFrom":[subQ1,subQ0]});Q4=makeQuery(id+"F21.imprint","IMPRINT",FACE,{"disambiguationData":[TD([[makeQuery(id+"F21.imprint","IMPRINT",EDGE,{"disambiguationData":[TD([[subQ2,1.0]])],"derivedFrom":subQ1}),1.0]])]});}
            extrude(context, id + "F25", {"entities" : qUnion([Q0, Q1, Q2, Q3, Q4]), "operationType" : NewBodyOperationType.REMOVE, "depth" : 8 * mm, "offsetDistance" : 25 * mm});
        }
    });
